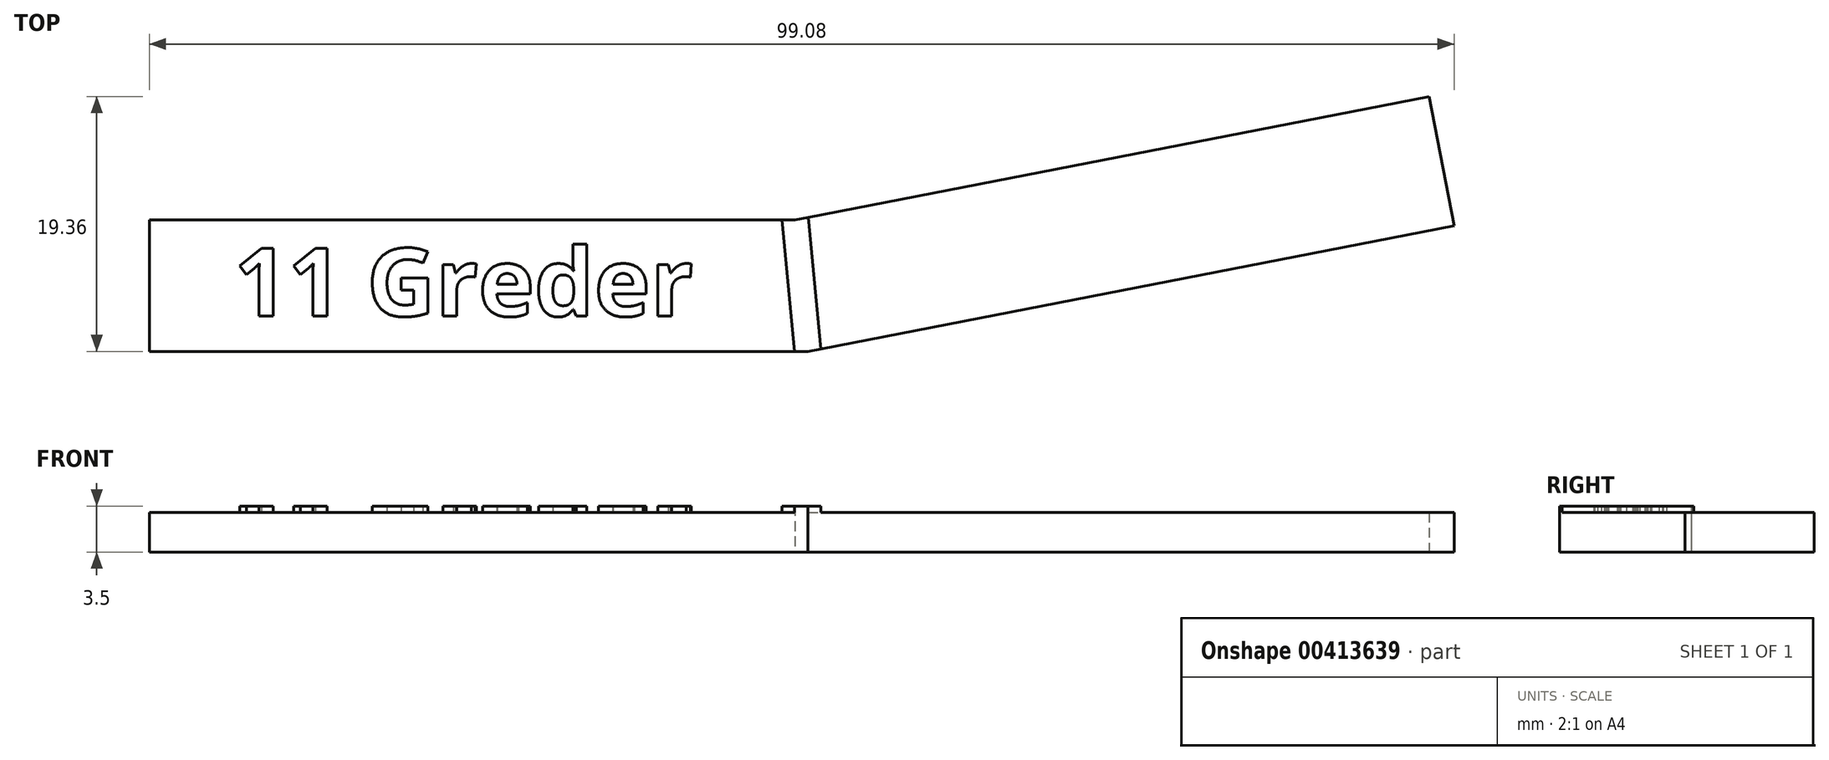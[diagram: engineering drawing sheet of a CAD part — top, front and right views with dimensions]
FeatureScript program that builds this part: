
annotation { "Feature Type Name" : "Feature", "Feature Type Description" : "" }
export const myFeature = defineFeature(function(context is Context, id is Id, definition is map)
    precondition{}
    {
        {
            var Q0;
            Q0=qCreatedBy(makeId("Top.planeOp"),FACE);
            var sketch = newSketch(context, id + "F0", { "sketchPlane" : qUnion([Q0])});
            skLineSegment(sketch, "E0", {"start": v(-50, 0) * mm, "end": v(0, 0) * mm});
            skLineSegment(sketch, "E1", {"start": v(0, 0) * mm, "end": v(49.08, 9.54) * mm});
            skLineSegment(sketch, "E2.0", {"start": v(-0.96, 10) * mm, "end": v(47.17, 19.36) * mm});
            skLineSegment(sketch, "E2.1", {"start": v(-50, 10) * mm, "end": v(-0.96, 10) * mm});
            skLineSegment(sketch, "E3", {"start": v(47.17, 19.36) * mm, "end": v(49.08, 9.54) * mm});
            skLineSegment(sketch, "E4", {"start": v(-50, 10) * mm, "end": v(-50, 0) * mm});
            skSolve(sketch);
        }
        {
            var Q0;
            Q0=makeQuery(id+"F0.imprint","IMPRINT",FACE,{"disambiguationData":[TD([[makeQuery(id+"F0.imprint","IMPRINT",EDGE,{"derivedFrom":sQuery(id+"F0.wireOp",EDGE,"E0")}),1.0]])]});
            extrude(context, id + "F1", {"entities" : qUnion([Q0]), "depth" : 3 * mm, "offsetDistance" : 25 * mm});
        }
        {
            var Q0;
            Q0=makeQuery(id+"F1.opExtrude","CAP_FACE",FACE,{"disambiguationData":[OSD([sQuery(id+"F0.wireOp",EDGE,"E0"),sQuery(id+"F0.wireOp",EDGE,"E1"),sQuery(id+"F0.wireOp",EDGE,"E2.0"),sQuery(id+"F0.wireOp",EDGE,"E2.1"),sQuery(id+"F0.wireOp",EDGE,"E3"),sQuery(id+"F0.wireOp",EDGE,"E4")])],"isStart":false});
            var sketch = newSketch(context, id + "F2", { "sketchPlane" : qUnion([Q0])});
            skText(sketch, "E5", { "text": "11 Greder", "fontName": "OpenSans-Bold.ttf"});
            skLineSegment(sketch, "E6", {"start": v(-0.96, 10) * mm, "end": v(0, 0) * mm});
            skLineSegment(sketch, "E7.0", {"start": v(-1.96, 9.9) * mm, "end": v(-1, -0.1) * mm});
            skLineSegment(sketch, "E8.0", {"start": v(0.03, 10.1) * mm, "end": v(1, 0.1) * mm});
            skLineSegment(sketch, "E9", {"start": v(-1.96, 9.9) * mm, "end": v(-1.97, 10) * mm});
            skLineSegment(sketch, "E10", {"start": v(0.03, 10.1) * mm, "end": v(0.02, 10.2) * mm});
            const initialGuessF2  = {"E5": [-0.04358, 0.00268, 1, 0, 0.00518]};
            skSetInitialGuess(sketch, initialGuessF2);
            skSolve(sketch);
        }
        {
            var Q0;
            Q0=makeQuery(id+"F2.imprint","IMPRINT",FACE,{"disambiguationData":[TD([[makeQuery(id+"F2.imprint","IMPRINT",EDGE,{"derivedFrom":sQuery(id+"F2.wireOp",EDGE,"E5.sketch_text.stroke-0")}),-1.0]])]});
            var Q1;
            Q1=makeQuery(id+"F2.imprint","IMPRINT",FACE,{"disambiguationData":[TD([[makeQuery(id+"F2.imprint","IMPRINT",EDGE,{"derivedFrom":sQuery(id+"F2.wireOp",EDGE,"E5.sketch_text.stroke-10")}),-1.0]])]});
            var Q2;
            Q2=makeQuery(id+"F2.imprint","IMPRINT",FACE,{"disambiguationData":[TD([[makeQuery(id+"F2.imprint","IMPRINT",EDGE,{"derivedFrom":sQuery(id+"F2.wireOp",EDGE,"E5.sketch_text.stroke-20")}),-1.0]])]});
            var Q3;
            Q3=makeQuery(id+"F2.imprint","IMPRINT",FACE,{"disambiguationData":[TD([[makeQuery(id+"F2.imprint","IMPRINT",EDGE,{"derivedFrom":sQuery(id+"F2.wireOp",EDGE,"E5.sketch_text.stroke-39")}),-1.0]])]});
            var Q4;
            Q4=makeQuery(id+"F2.imprint","IMPRINT",FACE,{"disambiguationData":[TD([[makeQuery(id+"F2.imprint","IMPRINT",EDGE,{"derivedFrom":sQuery(id+"F2.wireOp",EDGE,"E5.sketch_text.stroke-115")}),-1.0]])]});
            var Q5;
            Q5=makeQuery(id+"F2.imprint","IMPRINT",FACE,{"disambiguationData":[TD([[makeQuery(id+"F2.imprint","IMPRINT",EDGE,{"derivedFrom":sQuery(id+"F2.wireOp",EDGE,"E5.sketch_text.stroke-52")}),-1.0]])]});
            var Q6;
            Q6=makeQuery(id+"F2.imprint","IMPRINT",FACE,{"disambiguationData":[TD([[makeQuery(id+"F2.imprint","IMPRINT",EDGE,{"derivedFrom":sQuery(id+"F2.wireOp",EDGE,"E5.sketch_text.stroke-95")}),-1.0]])]});
            var Q7;
            Q7=makeQuery(id+"F2.imprint","IMPRINT",FACE,{"disambiguationData":[TD([[makeQuery(id+"F2.imprint","IMPRINT",EDGE,{"derivedFrom":sQuery(id+"F2.wireOp",EDGE,"E5.sketch_text.stroke-72")}),-1.0]])]});
            var Q8;
            {var subQ0=sQuery(id+"F2.wireOp",EDGE,"E6");Q8=makeQuery(id+"F2.imprint","IMPRINT",FACE,{"disambiguationData":[TD([[makeQuery(id+"F2.imprint","IMPRINT",EDGE,{"derivedFrom":subQ0}),-1.0]])]});}
            var Q9;
            {var subQ0=sQuery(id+"F2.wireOp",EDGE,"E6");Q9=makeQuery(id+"F2.imprint","IMPRINT",FACE,{"disambiguationData":[TD([[makeQuery(id+"F2.imprint","IMPRINT",EDGE,{"derivedFrom":subQ0}),1.0]])]});}
            extrude(context, id + "F3", {"entities" : qUnion([Q0, Q1, Q2, Q3, Q4, Q5, Q6, Q7, Q8, Q9]), "operationType" : NewBodyOperationType.ADD, "depth" : 0.5 * mm, "offsetDistance" : 25 * mm});
        }
    });
